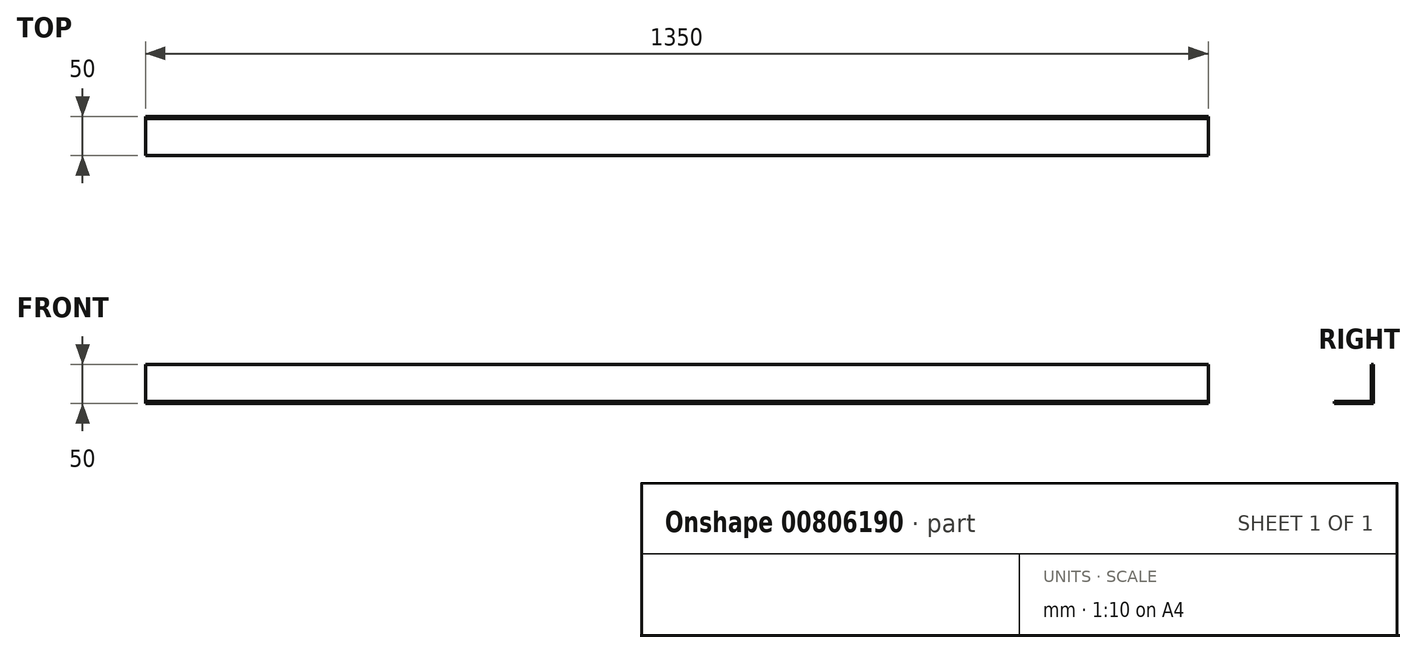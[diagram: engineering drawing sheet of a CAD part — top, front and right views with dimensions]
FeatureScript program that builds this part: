
annotation { "Feature Type Name" : "Feature", "Feature Type Description" : "" }
export const myFeature = defineFeature(function(context is Context, id is Id, definition is map)
    precondition{}
    {
        {
            var Q0;
            Q0=qCreatedBy(makeId("Right.planeOp"),FACE);
            var sketch = newSketch(context, id + "F0", { "sketchPlane" : qUnion([Q0])});
            skLineSegment(sketch, "E0", {"start": v(0, 0) * mm, "end": v(0, 50) * mm});
            skLineSegment(sketch, "E1", {"start": v(0, 0) * mm, "end": v(-50, 0) * mm});
            skLineSegment(sketch, "E2.0", {"start": v(-3, 3) * mm, "end": v(-3, 50) * mm});
            skLineSegment(sketch, "E2.1", {"start": v(-3, 3) * mm, "end": v(-50, 3) * mm});
            skLineSegment(sketch, "E3", {"start": v(0, 50) * mm, "end": v(-3, 50) * mm});
            skLineSegment(sketch, "E4", {"start": v(-50, 0) * mm, "end": v(-50, 3) * mm});
            skSolve(sketch);
        }
        {
            var Q0;
            Q0=qSketchRegion(id+"F0",true);
            extrude(context, id + "F1", {"entities" : qUnion([Q0]), "depth" : 1350 * mm, "offsetDistance" : 25 * mm});
        }
    });
